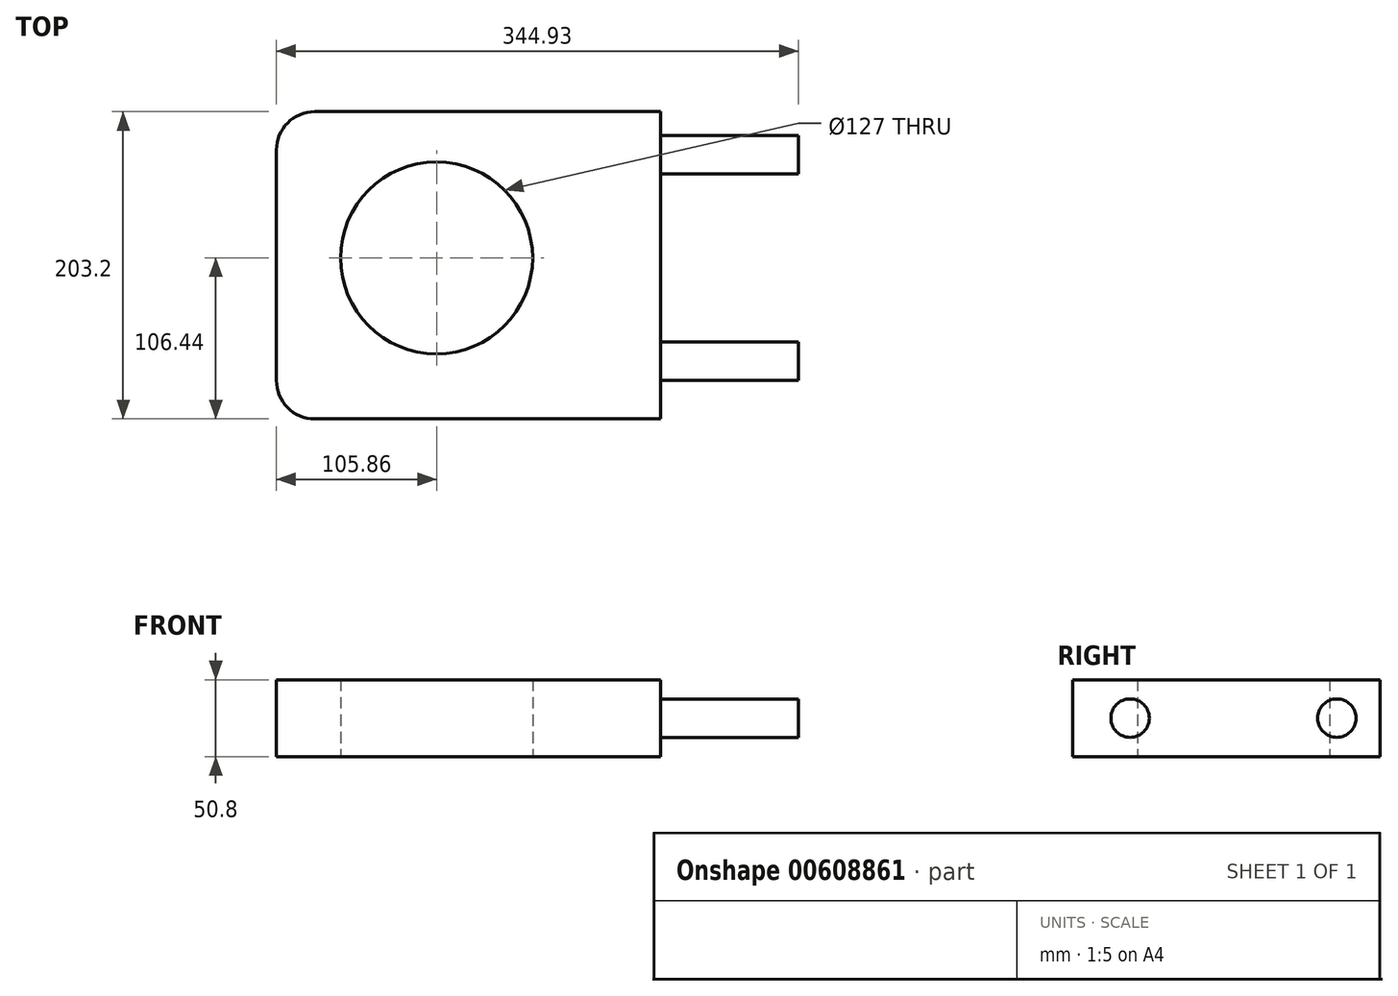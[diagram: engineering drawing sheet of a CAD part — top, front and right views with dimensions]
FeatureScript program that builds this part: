
annotation { "Feature Type Name" : "Feature", "Feature Type Description" : "" }
export const myFeature = defineFeature(function(context is Context, id is Id, definition is map)
    precondition{}
    {
        {
            var Q0;
            Q0=qCreatedBy(makeId("Top.planeOp"),FACE);
            var sketch = newSketch(context, id + "F0", { "sketchPlane" : qUnion([Q0])});
            skCircle(sketch, "E0", {"center": v(0, 0) * mm, "radius": 63.5 * mm});
            skLineSegment(sketch, "E1.bottom", {"start": v(-105.86, 96.76) * mm, "end": v(148.14, 96.76) * mm});
            skLineSegment(sketch, "E1.top", {"start": v(-105.86, -106.44) * mm, "end": v(148.14, -106.44) * mm});
            skLineSegment(sketch, "E1.left", {"start": v(-105.86, 96.76) * mm, "end": v(-105.86, -106.44) * mm});
            skLineSegment(sketch, "E1.right", {"start": v(148.14, 96.76) * mm, "end": v(148.14, -106.44) * mm});
            skSolve(sketch);
        }
        {
            var Q0;
            Q0=makeQuery(id+"F0.imprint","IMPRINT",FACE,{"disambiguationData":[TD([[makeQuery(id+"F0.imprint","IMPRINT",EDGE,{"derivedFrom":sQuery(id+"F0.wireOp",EDGE,"E0")}),-1.0]])]});
            extrude(context, id + "F1", {"entities" : qUnion([Q0]), "depth" : 50.8 * mm, "offsetDistance" : 25.4 * mm});
        }
        {
            var Q0;
            Q0=makeQuery(id+"F1.opExtrude","SWEPT_EDGE",EDGE,{"disambiguationData":[OSD([sQuery(id+"F0.wireOp",EDGE,"E1.bottom"),sQuery(id+"F0.wireOp",EDGE,"E1.left")])]});
            var Q1;
            Q1=makeQuery(id+"F1.opExtrude","SWEPT_EDGE",EDGE,{"disambiguationData":[OSD([sQuery(id+"F0.wireOp",EDGE,"E1.top"),sQuery(id+"F0.wireOp",EDGE,"E1.left")])]});
            fillet(context, id + "F2", {"entities" : qUnion([Q0, Q1]), "radius" : 25.4 * mm, "tangentPropagation" : true, "allowEdgeOverflow" : false});
        }
        {
            var Q0;
            Q0=makeQuery(id+"F1.opExtrude","SWEPT_FACE",FACE,{"disambiguationData":[OSD([sQuery(id+"F0.wireOp",EDGE,"E1.right")])]});
            var sketch = newSketch(context, id + "F3", { "sketchPlane" : qUnion([Q0])});
            skCircle(sketch, "E2", {"center": v(-68.34, 25.4) * mm, "radius": 12.7 * mm});
            skPoint(sketch, "E2.centerSnap0", {"position": v(-106.44, 25.4) * mm});
            skCircle(sketch, "E3.MirrorC", {"center": v(68.34, 25.4) * mm, "radius": 12.7 * mm});
            skSolve(sketch);
        }
        {
            var Q0;
            Q0 = qSketchRegion(id + "F3", true);
            extrude(context, id + "F4", {"entities" : qUnion([Q0]), "operationType" : NewBodyOperationType.ADD, "depth" : 90.93 * mm, "offsetDistance" : 25.4 * mm});
        }
    });
